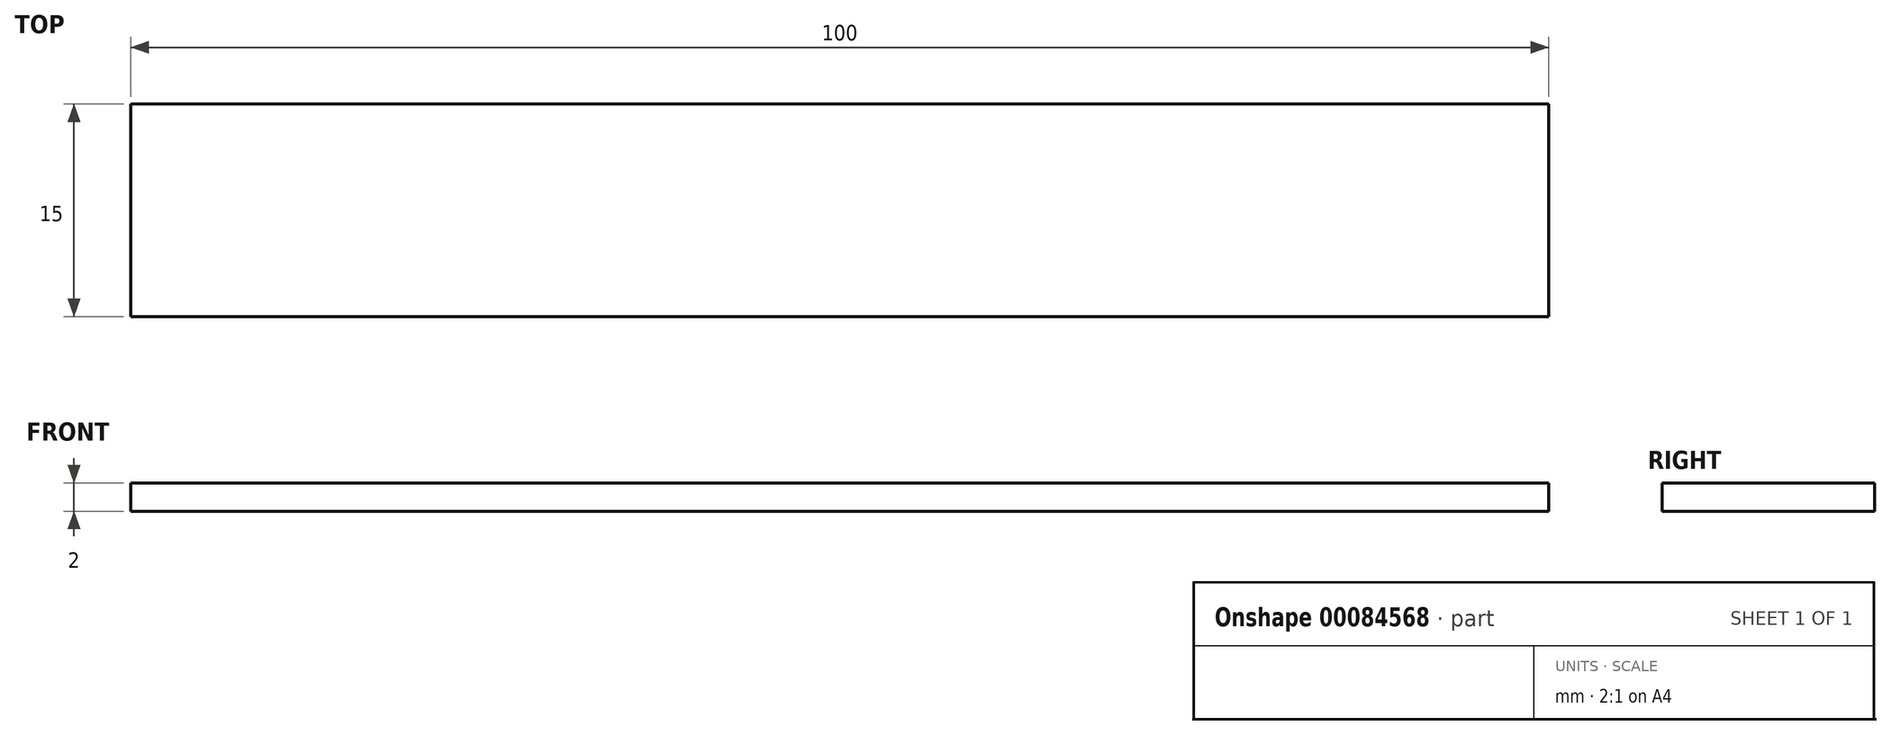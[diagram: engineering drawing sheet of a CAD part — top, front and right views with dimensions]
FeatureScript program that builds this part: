
annotation { "Feature Type Name" : "Feature", "Feature Type Description" : "" }
export const myFeature = defineFeature(function(context is Context, id is Id, definition is map)
    precondition{}
    {
        {
            var Q0;
            Q0=qCreatedBy(makeId("Top.planeOp"),FACE);
            var sketch = newSketch(context, id + "F0", { "sketchPlane" : qUnion([Q0]) });
            skLineSegment(sketch, "E0.bottom", {"start": v(0, 0) * mm, "end": v(100, 0) * mm});
            skLineSegment(sketch, "E0.top", {"start": v(0, 15) * mm, "end": v(100, 15) * mm});
            skLineSegment(sketch, "E0.left", {"start": v(0, 0) * mm, "end": v(0, 15) * mm});
            skLineSegment(sketch, "E0.right", {"start": v(100, 0) * mm, "end": v(100, 15) * mm});
            skSolve(sketch);
        }
        {
            var Q0;
            Q0 = qSketchRegion(id + "F0", true);
            extrude(context, id + "F1", {"entities" : qUnion([Q0]), "depth" : 2 * mm});
        }
    });
